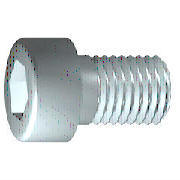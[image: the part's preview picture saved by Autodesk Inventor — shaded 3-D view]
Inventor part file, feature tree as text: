
AUTODESK INVENTOR PART (.ipt)
format: ipt  version: 2015 (Build 190159000, 159)  size: 194,560 bytes
history: native  units: mm (DEFAULTED — no unit token found)
features: sketch x2, extrude x1, plane x1, fillet x1
ambient origin geometry x7: Origin, YZ Plane, XY Plane, X Axis, Y Axis, Z Axis, Center Point
bodies: Solid1 (feature_tree), Body (feature_tree)
feature tree (5):
  extrude  "Slot"  Depth=6.0mm
  plane  "Work Plane1"
  fillet  "Fillet2"  Radius=6.0mm
  sketch  "Sketch1"  dims[d1=13.5mm d2=0.61355mm d3=6.0mm]
  sketch  "Sketch2"  dims[d4=3.0mm d5=60.0deg d6=6.0mm d7=6.0mm d8=5.773503mm d9=10.0mm d10=90.0deg d11=10.0mm d12=0.0mm d13=13.5mm d14=0.0mm d15=0.61345mm d16=0.61345mm d17=0.6mm d19=0.0mm d26=16.0mm d27=45.0deg d28=0.0mm d29=0.0mm d30=0.1mm]
